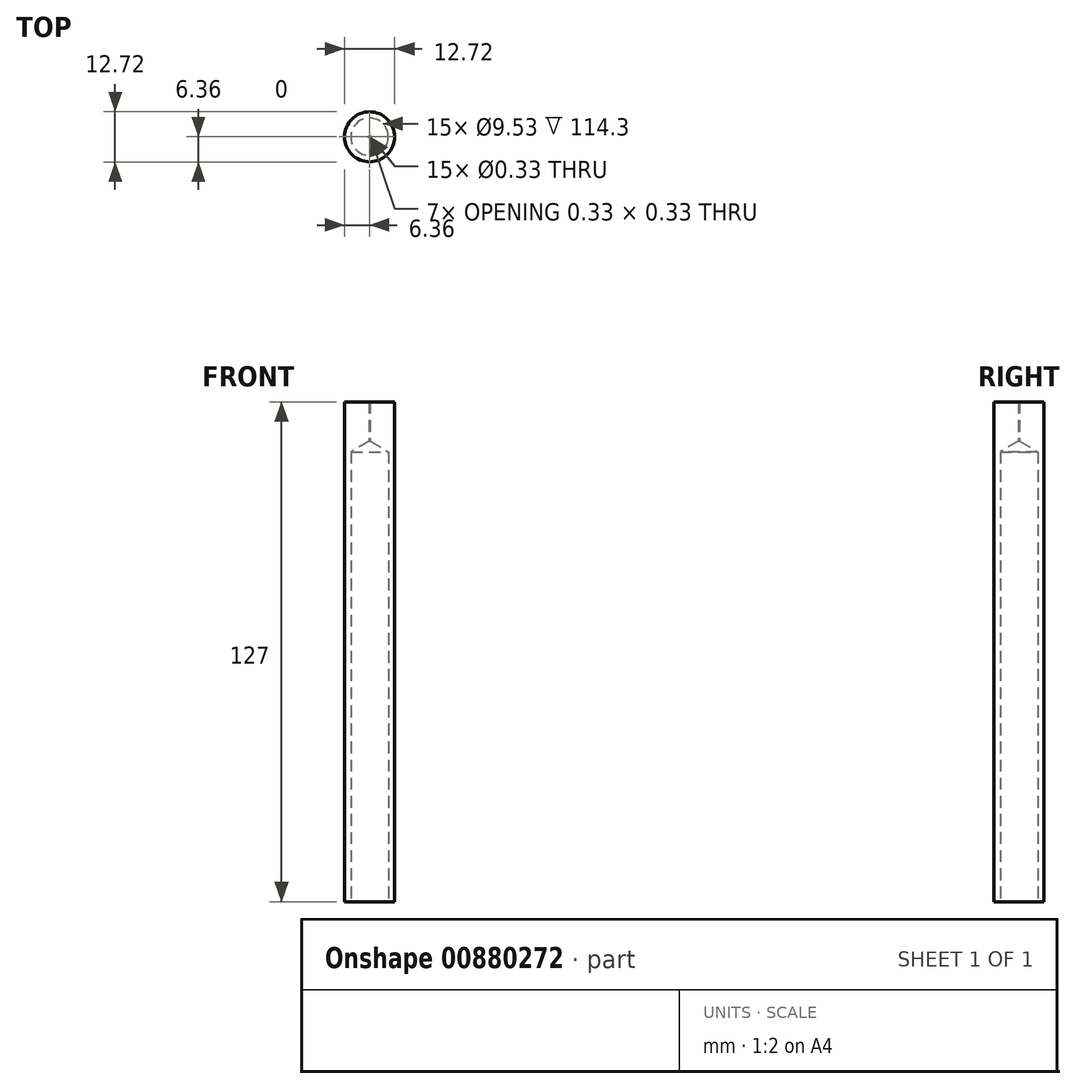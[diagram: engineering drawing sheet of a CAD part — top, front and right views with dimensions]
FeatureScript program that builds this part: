
annotation { "Feature Type Name" : "Feature", "Feature Type Description" : "" }
export const myFeature = defineFeature(function(context is Context, id is Id, definition is map)
    precondition{}
    {
        {
            var Q0;
            Q0=qCreatedBy(makeId("Top.planeOp"),FACE);
            var sketch = newSketch(context, id + "F0", { "sketchPlane" : qUnion([Q0])});
            skCircle(sketch, "E0", {"center": v(0, 0) * mm, "radius": 6.36 * mm});
            skSolve(sketch);
        }
        {
            var Q0;
            Q0=makeQuery(id+"F0.imprint","IMPRINT",FACE,{"disambiguationData":[TD([[makeQuery(id+"F0.imprint","IMPRINT",EDGE,{"derivedFrom":sQuery(id+"F0.wireOp",EDGE,"E0")}),1.0]])]});
            extrude(context, id + "F1", {"entities" : qUnion([Q0]), "depth" : 127 * mm, "offsetDistance" : 25.4 * mm});
        }
        {
            var Q0;
            Q0=sQuery(id+"F0.wireOp",VERTEX,"E0.center");
            var Q1;
            Q1=makeQuery(id+"F1.opExtrude","SWEPT_BODY",BODY,{"disambiguationData":[OSD([sQuery(id+"F0.wireOp",EDGE,"E0")])]});
            hole(context, id + "F2", {"style" : HoleStyle.SIMPLE, "endStyle" : HoleEndStyle.BLIND, "oppositeDirection" : true, "holeDiameter" : 9.52 * mm, "majorDiameter" : 6.35 * mm, "holeDepth" : 114.3 * mm, "isTappedThrough" : true, "tappedDepth" : 12.7 * mm, "tapClearance" : 3, "locations" : qUnion([Q0]), "scope" : qUnion([Q1])});
        }
        {
            var Q0;
            Q0=sQuery(id+"F0.wireOp",VERTEX,"E0.center");
            var Q1;
            Q1=makeQuery(id+"F1.opExtrude","SWEPT_BODY",BODY,{"disambiguationData":[OSD([sQuery(id+"F0.wireOp",EDGE,"E0")])]});
            hole(context, id + "F3", {"style" : HoleStyle.SIMPLE, "endStyle" : HoleEndStyle.THROUGH, "oppositeDirection" : true, "holeDiameter" : 0.33 * mm, "majorDiameter" : 6.35 * mm, "isTappedThrough" : true, "tappedDepth" : 12.7 * mm, "tapClearance" : 3, "locations" : qUnion([Q0]), "scope" : qUnion([Q1])});
        }
    });
